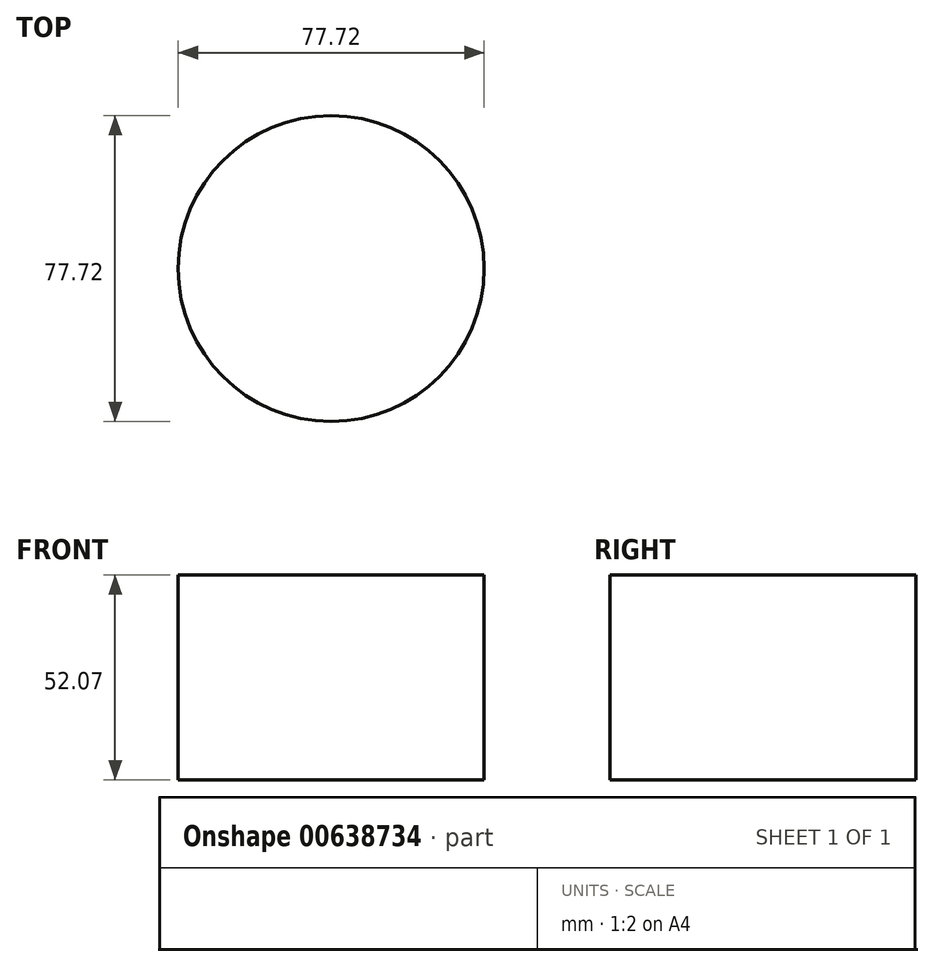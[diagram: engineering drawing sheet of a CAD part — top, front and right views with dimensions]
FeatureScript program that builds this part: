
annotation { "Feature Type Name" : "Feature", "Feature Type Description" : "" }
export const myFeature = defineFeature(function(context is Context, id is Id, definition is map)
    precondition{}
    {
        {
            var Q0;
            Q0=qCreatedBy(makeId("Top.planeOp"),FACE);
            var sketch = newSketch(context, id + "F0", { "sketchPlane" : qUnion([Q0])});
            skCircle(sketch, "E0", {"center": v(0, 0) * mm, "radius": 38.86 * mm});
            skSolve(sketch);
        }
        {
            var Q0;
            Q0=makeQuery(id+"F0.imprint","IMPRINT",FACE,{"disambiguationData":[TD([[makeQuery(id+"F0.imprint","IMPRINT",EDGE,{"derivedFrom":sQuery(id+"F0.wireOp",EDGE,"E0")}),1.0]])]});
            extrude(context, id + "F1", {"entities" : qUnion([Q0]), "depth" : 52.07 * mm, "offsetDistance" : 25.4 * mm});
        }
    });
